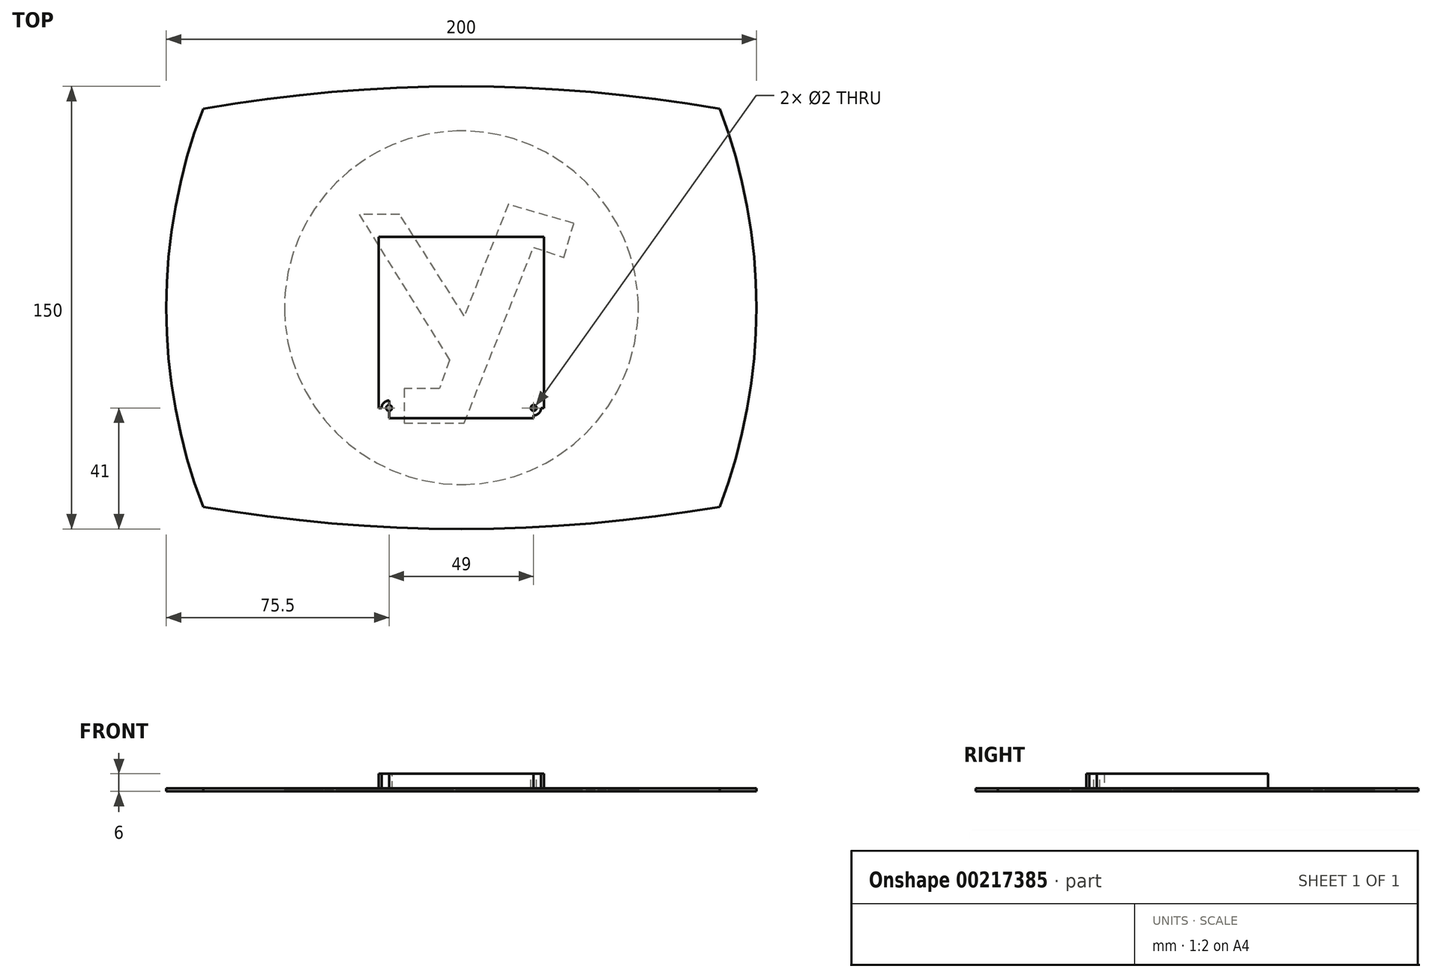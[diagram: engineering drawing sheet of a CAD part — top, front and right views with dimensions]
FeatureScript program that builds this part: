
annotation { "Feature Type Name" : "Feature", "Feature Type Description" : "" }
export const myFeature = defineFeature(function(context is Context, id is Id, definition is map)
    precondition{}
    {
        {
            var Q0;
            Q0=qCreatedBy(makeId("Top.planeOp"),FACE);
            var sketch = newSketch(context, id + "F0", { "sketchPlane" : qUnion([Q0])});
            skPoint(sketch, "E0.middle", {"position": v(0, 0) * mm});
            skPoint(sketch, "E1", {"position": v(0, 75) * mm});
            skPoint(sketch, "E2", {"position": v(0, -75) * mm});
            skPoint(sketch, "E3", {"position": v(100, 0) * mm});
            skPoint(sketch, "E4", {"position": v(-100, 0) * mm});
            skArc(sketch, "E5", {"start": v(87.5, 67.5) * mm, "mid": v(0, 75) * mm, "end": v(-87.5, 67.5) * mm});
            skArc(sketch, "E6", {"start": v(-87.5, 67.5) * mm, "mid": v(-100, 0) * mm, "end": v(-87.5, -67.5) * mm});
            skArc(sketch, "E7", {"start": v(87.5, -67.5) * mm, "mid": v(100, 0) * mm, "end": v(87.5, 67.5) * mm});
            skArc(sketch, "E8", {"start": v(-87.5, -67.5) * mm, "mid": v(0, -75) * mm, "end": v(87.5, -67.5) * mm});
            skPoint(sketch, "E9.orphan", {"position": v(-100, 75) * mm});
            skPoint(sketch, "E10.orphan", {"position": v(100, 75) * mm});
            skPoint(sketch, "E11.orphan", {"position": v(100, -75) * mm});
            skPoint(sketch, "E12.right.end.orphan", {"position": v(-100, -75) * mm});
            skPoint(sketch, "E13.trimOffspring.start.orphan", {"position": v(-74.5, 62.5) * mm});
            skPoint(sketch, "E14.orphan", {"position": v(-82.5, 62.5) * mm});
            skPoint(sketch, "E15.right.start.orphan", {"position": v(-82.5, -53.5) * mm});
            skPoint(sketch, "E16.trimOffspring.end.orphan", {"position": v(-82.5, -62.5) * mm});
            skPoint(sketch, "E17.trimOffspring.end.orphan", {"position": v(-74.5, -62.5) * mm});
            skPoint(sketch, "E0.top.end.orphan", {"position": v(74.5, -62.5) * mm});
            skPoint(sketch, "E15.left.end.orphan", {"position": v(82.5, 53.5) * mm});
            skPoint(sketch, "E15.left.start.orphan", {"position": v(82.5, -53.5) * mm});
            skPoint(sketch, "E18.orphan", {"position": v(82.5, -62.5) * mm});
            skPoint(sketch, "E0.bottom.end.orphan", {"position": v(74.5, 62.5) * mm});
            skPoint(sketch, "E0.bottom.start.orphan", {"position": v(82.5, 62.5) * mm});
            skPoint(sketch, "E0.right.start.orphan", {"position": v(-82.5, 53.5) * mm});
            skSolve(sketch);
        }
        {
            var Q0;
            Q0=makeQuery(id+"F0.imprint","IMPRINT",FACE,{"disambiguationData":[TD([[makeQuery(id+"F0.imprint","IMPRINT",EDGE,{"derivedFrom":sQuery(id+"F0.wireOp",EDGE,"E5")}),1.0]])]});
            extrude(context, id + "F1", {"entities" : qUnion([Q0]), "depth" : 1 * mm});
        }
        {
            var Q0;
            Q0=makeQuery(id+"F1.opExtrude","CAP_FACE",FACE,{"disambiguationData":[OSD([sQuery(id+"F0.wireOp",EDGE,"E5"),sQuery(id+"F0.wireOp",EDGE,"E6"),sQuery(id+"F0.wireOp",EDGE,"E7"),sQuery(id+"F0.wireOp",EDGE,"E8")])],"isStart":true});
            var sketch = newSketch(context, id + "F2", { "sketchPlane" : qUnion([Q0])});
            skLineSegment(sketch, "E19", {"start": v(15.93, -35.02) * mm, "end": v(1, 2.83) * mm});
            skLineSegment(sketch, "E20", {"start": v(1, 2.83) * mm, "end": v(-20.9, -31.67) * mm});
            skLineSegment(sketch, "E21", {"start": v(-20.9, -31.67) * mm, "end": v(-34.63, -31.67) * mm});
            skLineSegment(sketch, "E22", {"start": v(-34.63, -31.67) * mm, "end": v(-4.05, 17.71) * mm});
            skLineSegment(sketch, "E23", {"start": v(-4.05, 17.71) * mm, "end": v(-7.48, 27.47) * mm});
            skLineSegment(sketch, "E24", {"start": v(-7.48, 27.47) * mm, "end": v(-19.4, 27.47) * mm});
            skLineSegment(sketch, "E25", {"start": v(-19.4, 27.47) * mm, "end": v(-19.4, 39.1) * mm});
            skLineSegment(sketch, "E26", {"start": v(-19.4, 39.1) * mm, "end": v(1, 39.1) * mm});
            skLineSegment(sketch, "E27", {"start": v(1, 39.1) * mm, "end": v(24.4, -20.44) * mm});
            skLineSegment(sketch, "E28", {"start": v(24.4, -20.44) * mm, "end": v(34.7, -17.08) * mm});
            skLineSegment(sketch, "E29", {"start": v(34.7, -17.08) * mm, "end": v(38.13, -28.61) * mm});
            skLineSegment(sketch, "E30", {"start": v(38.13, -28.61) * mm, "end": v(15.93, -35.02) * mm});
            skLineSegment(sketch, "E31", {"start": v(59.94, 0) * mm, "end": v(59.94, -1.53) * mm});
            skLineSegment(sketch, "E32", {"start": v(59.94, -1.53) * mm, "end": v(59.63, -6.13) * mm});
            skLineSegment(sketch, "E33", {"start": v(59.63, -6.13) * mm, "end": v(58.72, -12.08) * mm});
            skLineSegment(sketch, "E34", {"start": v(58.72, -12.08) * mm, "end": v(57.24, -17.82) * mm});
            skLineSegment(sketch, "E35", {"start": v(57.24, -17.82) * mm, "end": v(55.23, -23.33) * mm});
            skLineSegment(sketch, "E36", {"start": v(55.23, -23.33) * mm, "end": v(52.7, -28.57) * mm});
            skLineSegment(sketch, "E37", {"start": v(52.7, -28.57) * mm, "end": v(49.7, -33.51) * mm});
            skLineSegment(sketch, "E38", {"start": v(49.7, -33.51) * mm, "end": v(46.25, -38.13) * mm});
            skLineSegment(sketch, "E39", {"start": v(46.25, -38.13) * mm, "end": v(42.38, -42.39) * mm});
            skLineSegment(sketch, "E40", {"start": v(42.38, -42.39) * mm, "end": v(38.13, -46.25) * mm});
            skLineSegment(sketch, "E41", {"start": v(38.13, -46.25) * mm, "end": v(33.51, -49.7) * mm});
            skLineSegment(sketch, "E42", {"start": v(33.51, -49.7) * mm, "end": v(28.57, -52.7) * mm});
            skLineSegment(sketch, "E43", {"start": v(28.57, -52.7) * mm, "end": v(23.33, -55.23) * mm});
            skLineSegment(sketch, "E44", {"start": v(23.33, -55.23) * mm, "end": v(17.82, -57.24) * mm});
            skLineSegment(sketch, "E45", {"start": v(17.82, -57.24) * mm, "end": v(12.08, -58.72) * mm});
            skLineSegment(sketch, "E46", {"start": v(12.08, -58.72) * mm, "end": v(6.13, -59.63) * mm});
            skLineSegment(sketch, "E47", {"start": v(6.13, -59.63) * mm, "end": v(1.53, -59.94) * mm});
            skLineSegment(sketch, "E48", {"start": v(1.53, -59.94) * mm, "end": v(0, -59.94) * mm});
            skLineSegment(sketch, "E49", {"start": v(0, -59.94) * mm, "end": v(-1.53, -59.94) * mm});
            skLineSegment(sketch, "E50", {"start": v(-1.53, -59.94) * mm, "end": v(-6.13, -59.63) * mm});
            skLineSegment(sketch, "E51", {"start": v(-6.13, -59.63) * mm, "end": v(-12.08, -58.72) * mm});
            skLineSegment(sketch, "E52", {"start": v(-12.08, -58.72) * mm, "end": v(-17.83, -57.24) * mm});
            skLineSegment(sketch, "E53", {"start": v(-17.83, -57.24) * mm, "end": v(-23.33, -55.23) * mm});
            skLineSegment(sketch, "E54", {"start": v(-23.33, -55.23) * mm, "end": v(-28.57, -52.7) * mm});
            skLineSegment(sketch, "E55", {"start": v(-28.57, -52.7) * mm, "end": v(-33.51, -49.7) * mm});
            skLineSegment(sketch, "E56", {"start": v(-33.51, -49.7) * mm, "end": v(-38.13, -46.25) * mm});
            skLineSegment(sketch, "E57", {"start": v(-38.13, -46.25) * mm, "end": v(-42.39, -42.39) * mm});
            skLineSegment(sketch, "E58", {"start": v(-42.39, -42.39) * mm, "end": v(-46.25, -38.13) * mm});
            skLineSegment(sketch, "E59", {"start": v(-46.25, -38.13) * mm, "end": v(-49.7, -33.51) * mm});
            skLineSegment(sketch, "E60", {"start": v(-49.7, -33.51) * mm, "end": v(-52.7, -28.57) * mm});
            skLineSegment(sketch, "E61", {"start": v(-52.7, -28.57) * mm, "end": v(-55.23, -23.33) * mm});
            skLineSegment(sketch, "E62", {"start": v(-55.23, -23.33) * mm, "end": v(-57.25, -17.82) * mm});
            skLineSegment(sketch, "E63", {"start": v(-57.25, -17.82) * mm, "end": v(-58.72, -12.08) * mm});
            skLineSegment(sketch, "E64", {"start": v(-58.72, -12.08) * mm, "end": v(-59.63, -6.13) * mm});
            skLineSegment(sketch, "E65", {"start": v(-59.63, -6.13) * mm, "end": v(-59.94, -1.53) * mm});
            skLineSegment(sketch, "E66", {"start": v(-59.94, -1.53) * mm, "end": v(-59.94, 0) * mm});
            skLineSegment(sketch, "E67", {"start": v(-59.94, 0) * mm, "end": v(-59.94, 1.53) * mm});
            skLineSegment(sketch, "E68", {"start": v(-59.94, 1.53) * mm, "end": v(-59.63, 6.13) * mm});
            skLineSegment(sketch, "E69", {"start": v(-59.63, 6.13) * mm, "end": v(-58.72, 12.08) * mm});
            skLineSegment(sketch, "E70", {"start": v(-58.72, 12.08) * mm, "end": v(-57.25, 17.82) * mm});
            skLineSegment(sketch, "E71", {"start": v(-57.25, 17.82) * mm, "end": v(-55.23, 23.33) * mm});
            skLineSegment(sketch, "E72", {"start": v(-55.23, 23.33) * mm, "end": v(-52.7, 28.57) * mm});
            skLineSegment(sketch, "E73", {"start": v(-52.7, 28.57) * mm, "end": v(-49.7, 33.51) * mm});
            skLineSegment(sketch, "E74", {"start": v(-49.7, 33.51) * mm, "end": v(-46.25, 38.13) * mm});
            skLineSegment(sketch, "E75", {"start": v(-46.25, 38.13) * mm, "end": v(-42.39, 42.38) * mm});
            skLineSegment(sketch, "E76", {"start": v(-42.39, 42.38) * mm, "end": v(-38.13, 46.25) * mm});
            skLineSegment(sketch, "E77", {"start": v(-38.13, 46.25) * mm, "end": v(-33.52, 49.7) * mm});
            skLineSegment(sketch, "E78", {"start": v(-33.52, 49.7) * mm, "end": v(-28.57, 52.7) * mm});
            skLineSegment(sketch, "E79", {"start": v(-28.57, 52.7) * mm, "end": v(-23.33, 55.23) * mm});
            skLineSegment(sketch, "E80", {"start": v(-23.33, 55.23) * mm, "end": v(-17.83, 57.25) * mm});
            skLineSegment(sketch, "E81", {"start": v(-17.83, 57.25) * mm, "end": v(-12.08, 58.72) * mm});
            skLineSegment(sketch, "E82", {"start": v(-12.08, 58.72) * mm, "end": v(-6.13, 59.63) * mm});
            skLineSegment(sketch, "E83", {"start": v(-6.13, 59.63) * mm, "end": v(-1.53, 59.94) * mm});
            skLineSegment(sketch, "E84", {"start": v(-1.53, 59.94) * mm, "end": v(0, 59.94) * mm});
            skLineSegment(sketch, "E85", {"start": v(0, 59.94) * mm, "end": v(1.53, 59.94) * mm});
            skLineSegment(sketch, "E86", {"start": v(1.53, 59.94) * mm, "end": v(6.13, 59.63) * mm});
            skLineSegment(sketch, "E87", {"start": v(6.13, 59.63) * mm, "end": v(12.08, 58.72) * mm});
            skLineSegment(sketch, "E88", {"start": v(12.08, 58.72) * mm, "end": v(17.82, 57.25) * mm});
            skLineSegment(sketch, "E89", {"start": v(17.82, 57.25) * mm, "end": v(23.33, 55.23) * mm});
            skLineSegment(sketch, "E90", {"start": v(23.33, 55.23) * mm, "end": v(28.57, 52.7) * mm});
            skLineSegment(sketch, "E91", {"start": v(28.57, 52.7) * mm, "end": v(33.51, 49.7) * mm});
            skLineSegment(sketch, "E92", {"start": v(33.51, 49.7) * mm, "end": v(38.13, 46.25) * mm});
            skLineSegment(sketch, "E93", {"start": v(38.13, 46.25) * mm, "end": v(42.38, 42.38) * mm});
            skLineSegment(sketch, "E94", {"start": v(42.38, 42.38) * mm, "end": v(46.25, 38.13) * mm});
            skLineSegment(sketch, "E95", {"start": v(46.25, 38.13) * mm, "end": v(49.7, 33.51) * mm});
            skLineSegment(sketch, "E96", {"start": v(49.7, 33.51) * mm, "end": v(52.7, 28.57) * mm});
            skLineSegment(sketch, "E97", {"start": v(52.7, 28.57) * mm, "end": v(55.23, 23.33) * mm});
            skLineSegment(sketch, "E98", {"start": v(55.23, 23.33) * mm, "end": v(57.24, 17.82) * mm});
            skLineSegment(sketch, "E99", {"start": v(57.24, 17.82) * mm, "end": v(58.72, 12.08) * mm});
            skLineSegment(sketch, "E100", {"start": v(58.72, 12.08) * mm, "end": v(59.63, 6.13) * mm});
            skLineSegment(sketch, "E101", {"start": v(59.63, 6.13) * mm, "end": v(59.94, 1.53) * mm});
            skLineSegment(sketch, "E102", {"start": v(59.94, 1.53) * mm, "end": v(59.94, 0) * mm});
            skSolve(sketch);
        }
        {
            var Q0;
            Q0 = qSketchRegion(id + "F2", true);
            extrude(context, id + "F3", {"entities" : qUnion([Q0]), "operationType" : NewBodyOperationType.REMOVE, "oppositeDirection" : true, "depth" : .5 * mm});
        }
        {
            var Q0;
            Q0=makeQuery(id+"F1.opExtrude","CAP_FACE",FACE,{"disambiguationData":[OSD([sQuery(id+"F0.wireOp",EDGE,"E5"),sQuery(id+"F0.wireOp",EDGE,"E6"),sQuery(id+"F0.wireOp",EDGE,"E7"),sQuery(id+"F0.wireOp",EDGE,"E8")])],"isStart":false});
            var sketch = newSketch(context, id + "F4", { "sketchPlane" : qUnion([Q0])});
            skLineSegment(sketch, "E103.bottom", {"start": v(-28, 47.5) * mm, "end": v(28, 47.5) * mm});
            skLineSegment(sketch, "E103.top", {"start": v(-28, -37.5) * mm, "end": v(28, -37.5) * mm});
            skLineSegment(sketch, "E103.left", {"start": v(-28, 47.5) * mm, "end": v(-28, -37.5) * mm});
            skLineSegment(sketch, "E103.right", {"start": v(28, 47.5) * mm, "end": v(28, -37.5) * mm});
            skLineSegment(sketch, "E104", {"start": v(-28, -34) * mm, "end": v(28, -34) * mm});
            skLineSegment(sketch, "E105", {"start": v(-24.5, 47.5) * mm, "end": v(-24.5, -37.5) * mm});
            skLineSegment(sketch, "E106", {"start": v(24.5, 47.5) * mm, "end": v(24.5, -37.5) * mm});
            skLineSegment(sketch, "E107", {"start": v(-28, 24) * mm, "end": v(28, 24) * mm});
            skCircle(sketch, "E108", {"center": v(-24.5, 24) * mm, "radius": 2.5 * mm});
            skCircle(sketch, "E109", {"center": v(24.5, 24) * mm, "radius": 2.5 * mm});
            skCircle(sketch, "E110", {"center": v(24.5, -34) * mm, "radius": 2.5 * mm});
            skCircle(sketch, "E111", {"center": v(-24.5, -34) * mm, "radius": 2.5 * mm});
            skSolve(sketch);
        }
        {
            var Q0;
            {var subQ0=sQuery(id+"F4.wireOp",EDGE,"E111");var subQ1=sQuery(id+"F4.wireOp",EDGE,"E104");var subQ2=makeQuery(id+"F4.imprint","INTERSECT",VERTEX,{"disambiguationData":[OD(0.0)],"derivedFrom":[subQ1,subQ0]});Q0=makeQuery(id+"F4.imprint","IMPRINT",FACE,{"disambiguationData":[TD([[makeQuery(id+"F4.imprint","IMPRINT",EDGE,{"disambiguationData":[TD([[subQ2,-1.0]])],"derivedFrom":subQ1}),1.0]])]});}
            var Q1;
            {var subQ0=sQuery(id+"F4.wireOp",EDGE,"E105");var subQ1=sQuery(id+"F4.wireOp",EDGE,"E104");var subQ2=makeQuery(id+"F4.imprint","INTERSECT",VERTEX,{"derivedFrom":[subQ1,subQ0]});Q1=makeQuery(id+"F4.imprint","IMPRINT",FACE,{"disambiguationData":[TD([[makeQuery(id+"F4.imprint","IMPRINT",EDGE,{"disambiguationData":[TD([[subQ2,-1.0]])],"derivedFrom":subQ1}),1.0]])]});}
            var Q2;
            {var subQ0=sQuery(id+"F4.wireOp",EDGE,"E105");var subQ1=sQuery(id+"F4.wireOp",EDGE,"E104");var subQ2=makeQuery(id+"F4.imprint","INTERSECT",VERTEX,{"derivedFrom":[subQ1,subQ0]});Q2=makeQuery(id+"F4.imprint","IMPRINT",FACE,{"disambiguationData":[TD([[makeQuery(id+"F4.imprint","IMPRINT",EDGE,{"disambiguationData":[TD([[subQ2,-1.0]])],"derivedFrom":subQ1}),-1.0]])]});}
            var Q3;
            {var subQ0=sQuery(id+"F4.wireOp",EDGE,"E111");var subQ1=sQuery(id+"F4.wireOp",EDGE,"E104");var subQ2=makeQuery(id+"F4.imprint","INTERSECT",VERTEX,{"disambiguationData":[OD(0.0)],"derivedFrom":[subQ1,subQ0]});Q3=makeQuery(id+"F4.imprint","IMPRINT",FACE,{"disambiguationData":[TD([[makeQuery(id+"F4.imprint","IMPRINT",EDGE,{"disambiguationData":[TD([[subQ2,-1.0]])],"derivedFrom":subQ1}),-1.0]])]});}
            var Q4;
            {var subQ0=sQuery(id+"F4.wireOp",EDGE,"E108");var subQ1=sQuery(id+"F4.wireOp",EDGE,"E105");var subQ2=makeQuery(id+"F4.imprint","INTERSECT",VERTEX,{"disambiguationData":[OD(0.0)],"derivedFrom":[subQ1,subQ0]});Q4=makeQuery(id+"F4.imprint","IMPRINT",FACE,{"disambiguationData":[TD([[makeQuery(id+"F4.imprint","IMPRINT",EDGE,{"disambiguationData":[TD([[subQ2,-1.0]])],"derivedFrom":subQ1}),-1.0]])]});}
            var Q5;
            {var subQ0=sQuery(id+"F4.wireOp",EDGE,"E107");var subQ1=sQuery(id+"F4.wireOp",EDGE,"E105");var subQ2=makeQuery(id+"F4.imprint","INTERSECT",VERTEX,{"derivedFrom":[subQ1,subQ0]});Q5=makeQuery(id+"F4.imprint","IMPRINT",FACE,{"disambiguationData":[TD([[makeQuery(id+"F4.imprint","IMPRINT",EDGE,{"disambiguationData":[TD([[subQ2,-1.0]])],"derivedFrom":subQ1}),-1.0]])]});}
            var Q6;
            {var subQ0=sQuery(id+"F4.wireOp",EDGE,"E108");var subQ1=sQuery(id+"F4.wireOp",EDGE,"E105");var subQ2=makeQuery(id+"F4.imprint","INTERSECT",VERTEX,{"disambiguationData":[OD(0.0)],"derivedFrom":[subQ1,subQ0]});Q6=makeQuery(id+"F4.imprint","IMPRINT",FACE,{"disambiguationData":[TD([[makeQuery(id+"F4.imprint","IMPRINT",EDGE,{"disambiguationData":[TD([[subQ2,-1.0]])],"derivedFrom":subQ1}),1.0]])]});}
            var Q7;
            {var subQ0=sQuery(id+"F4.wireOp",EDGE,"E107");var subQ1=sQuery(id+"F4.wireOp",EDGE,"E105");var subQ2=makeQuery(id+"F4.imprint","INTERSECT",VERTEX,{"derivedFrom":[subQ1,subQ0]});Q7=makeQuery(id+"F4.imprint","IMPRINT",FACE,{"disambiguationData":[TD([[makeQuery(id+"F4.imprint","IMPRINT",EDGE,{"disambiguationData":[TD([[subQ2,-1.0]])],"derivedFrom":subQ1}),1.0]])]});}
            var Q8;
            {var subQ0=sQuery(id+"F4.wireOp",EDGE,"E110");var subQ1=sQuery(id+"F4.wireOp",EDGE,"E104");var subQ2=makeQuery(id+"F4.imprint","INTERSECT",VERTEX,{"disambiguationData":[OD(0.0)],"derivedFrom":[subQ1,subQ0]});Q8=makeQuery(id+"F4.imprint","IMPRINT",FACE,{"disambiguationData":[TD([[makeQuery(id+"F4.imprint","IMPRINT",EDGE,{"disambiguationData":[TD([[subQ2,-1.0]])],"derivedFrom":subQ1}),1.0]])]});}
            var Q9;
            {var subQ0=sQuery(id+"F4.wireOp",EDGE,"E110");var subQ1=sQuery(id+"F4.wireOp",EDGE,"E104");var subQ2=makeQuery(id+"F4.imprint","INTERSECT",VERTEX,{"disambiguationData":[OD(0.0)],"derivedFrom":[subQ1,subQ0]});Q9=makeQuery(id+"F4.imprint","IMPRINT",FACE,{"disambiguationData":[TD([[makeQuery(id+"F4.imprint","IMPRINT",EDGE,{"disambiguationData":[TD([[subQ2,-1.0]])],"derivedFrom":subQ1}),-1.0]])]});}
            var Q10;
            {var subQ0=sQuery(id+"F4.wireOp",EDGE,"E106");var subQ1=sQuery(id+"F4.wireOp",EDGE,"E104");var subQ2=makeQuery(id+"F4.imprint","INTERSECT",VERTEX,{"derivedFrom":[subQ1,subQ0]});Q10=makeQuery(id+"F4.imprint","IMPRINT",FACE,{"disambiguationData":[TD([[makeQuery(id+"F4.imprint","IMPRINT",EDGE,{"disambiguationData":[TD([[subQ2,-1.0]])],"derivedFrom":subQ1}),1.0]])]});}
            var Q11;
            {var subQ0=sQuery(id+"F4.wireOp",EDGE,"E106");var subQ1=sQuery(id+"F4.wireOp",EDGE,"E104");var subQ2=makeQuery(id+"F4.imprint","INTERSECT",VERTEX,{"derivedFrom":[subQ1,subQ0]});Q11=makeQuery(id+"F4.imprint","IMPRINT",FACE,{"disambiguationData":[TD([[makeQuery(id+"F4.imprint","IMPRINT",EDGE,{"disambiguationData":[TD([[subQ2,-1.0]])],"derivedFrom":subQ1}),-1.0]])]});}
            var Q12;
            {var subQ0=sQuery(id+"F4.wireOp",EDGE,"E109");var subQ1=sQuery(id+"F4.wireOp",EDGE,"E106");var subQ2=makeQuery(id+"F4.imprint","INTERSECT",VERTEX,{"disambiguationData":[OD(0.0)],"derivedFrom":[subQ1,subQ0]});Q12=makeQuery(id+"F4.imprint","IMPRINT",FACE,{"disambiguationData":[TD([[makeQuery(id+"F4.imprint","IMPRINT",EDGE,{"disambiguationData":[TD([[subQ2,-1.0]])],"derivedFrom":subQ1}),-1.0]])]});}
            var Q13;
            {var subQ0=sQuery(id+"F4.wireOp",EDGE,"E109");var subQ1=sQuery(id+"F4.wireOp",EDGE,"E106");var subQ2=makeQuery(id+"F4.imprint","INTERSECT",VERTEX,{"disambiguationData":[OD(0.0)],"derivedFrom":[subQ1,subQ0]});Q13=makeQuery(id+"F4.imprint","IMPRINT",FACE,{"disambiguationData":[TD([[makeQuery(id+"F4.imprint","IMPRINT",EDGE,{"disambiguationData":[TD([[subQ2,-1.0]])],"derivedFrom":subQ1}),1.0]])]});}
            var Q14;
            {var subQ0=sQuery(id+"F4.wireOp",EDGE,"E107");var subQ1=sQuery(id+"F4.wireOp",EDGE,"E106");var subQ2=makeQuery(id+"F4.imprint","INTERSECT",VERTEX,{"derivedFrom":[subQ1,subQ0]});Q14=makeQuery(id+"F4.imprint","IMPRINT",FACE,{"disambiguationData":[TD([[makeQuery(id+"F4.imprint","IMPRINT",EDGE,{"disambiguationData":[TD([[subQ2,-1.0]])],"derivedFrom":subQ1}),1.0]])]});}
            var Q15;
            {var subQ0=sQuery(id+"F4.wireOp",EDGE,"E107");var subQ1=sQuery(id+"F4.wireOp",EDGE,"E106");var subQ2=makeQuery(id+"F4.imprint","INTERSECT",VERTEX,{"derivedFrom":[subQ1,subQ0]});Q15=makeQuery(id+"F4.imprint","IMPRINT",FACE,{"disambiguationData":[TD([[makeQuery(id+"F4.imprint","IMPRINT",EDGE,{"disambiguationData":[TD([[subQ2,-1.0]])],"derivedFrom":subQ1}),-1.0]])]});}
            extrude(context, id + "F5", {"entities" : qUnion([Q0, Q1, Q2, Q3, Q4, Q5, Q6, Q7, Q8, Q9, Q10, Q11, Q12, Q13, Q14, Q15]), "operationType" : NewBodyOperationType.ADD, "depth" : 5 * mm});
        }
        {
            var Q0;
            Q0=makeQuery(id+"F5.opExtrude","CAP_FACE",FACE,{"disambiguationData":[OSD([sQuery(id+"F4.wireOp",EDGE,"E108")])],"isStart":false});
            var sketch = newSketch(context, id + "F6", { "sketchPlane" : qUnion([Q0])});
            skPoint(sketch, "E112", {"position": v(-24.5, 24) * mm});
            skSolve(sketch);
        }
        {
            var Q0;
            Q0=makeQuery(id+"F5.opExtrude","CAP_FACE",FACE,{"disambiguationData":[OSD([sQuery(id+"F4.wireOp",EDGE,"E109")])],"isStart":false});
            var sketch = newSketch(context, id + "F7", { "sketchPlane" : qUnion([Q0])});
            skPoint(sketch, "E113", {"position": v(24.5, 24) * mm});
            skSolve(sketch);
        }
        {
            var Q0;
            Q0=makeQuery(id+"F5.opExtrude","CAP_FACE",FACE,{"disambiguationData":[OSD([sQuery(id+"F4.wireOp",EDGE,"E111")])],"isStart":false});
            var sketch = newSketch(context, id + "F8", { "sketchPlane" : qUnion([Q0])});
            skPoint(sketch, "E114", {"position": v(-24.5, -34) * mm});
            skSolve(sketch);
        }
        {
            var Q0;
            Q0=makeQuery(id+"F5.opExtrude","CAP_FACE",FACE,{"disambiguationData":[OSD([sQuery(id+"F4.wireOp",EDGE,"E110")])],"isStart":false});
            var sketch = newSketch(context, id + "F9", { "sketchPlane" : qUnion([Q0])});
            skPoint(sketch, "E115", {"position": v(24.5, -34) * mm});
            skSolve(sketch);
        }
        {
            var Q0;
            Q0=sQuery(id+"F6.wireOp",VERTEX,"E112");
            var Q1;
            Q1=sQuery(id+"F7.wireOp",VERTEX,"E113");
            var Q2;
            Q2=sQuery(id+"F8.wireOp",VERTEX,"E114");
            var Q3;
            Q3=sQuery(id+"F9.wireOp",VERTEX,"E115");
            var Q4;
            Q4=makeQuery(id+"F1.opExtrude","SWEPT_BODY",BODY,{"disambiguationData":[OSD([sQuery(id+"F0.wireOp",EDGE,"E5"),sQuery(id+"F0.wireOp",EDGE,"E6"),sQuery(id+"F0.wireOp",EDGE,"E7"),sQuery(id+"F0.wireOp",EDGE,"E8")])]});
            hole(context, id + "F10", {"style" : HoleStyle.SIMPLE, "endStyle" : HoleEndStyle.BLIND, "holeDiameter" : 2 * mm, "holeDepth" : 5 * mm, "isTappedThrough" : true, "tappedDepth" : 12 * mm, "tapClearance" : 3, "locations" : qUnion([Q0, Q1, Q2, Q3]), "scope" : qUnion([Q4])});
        }
    });
